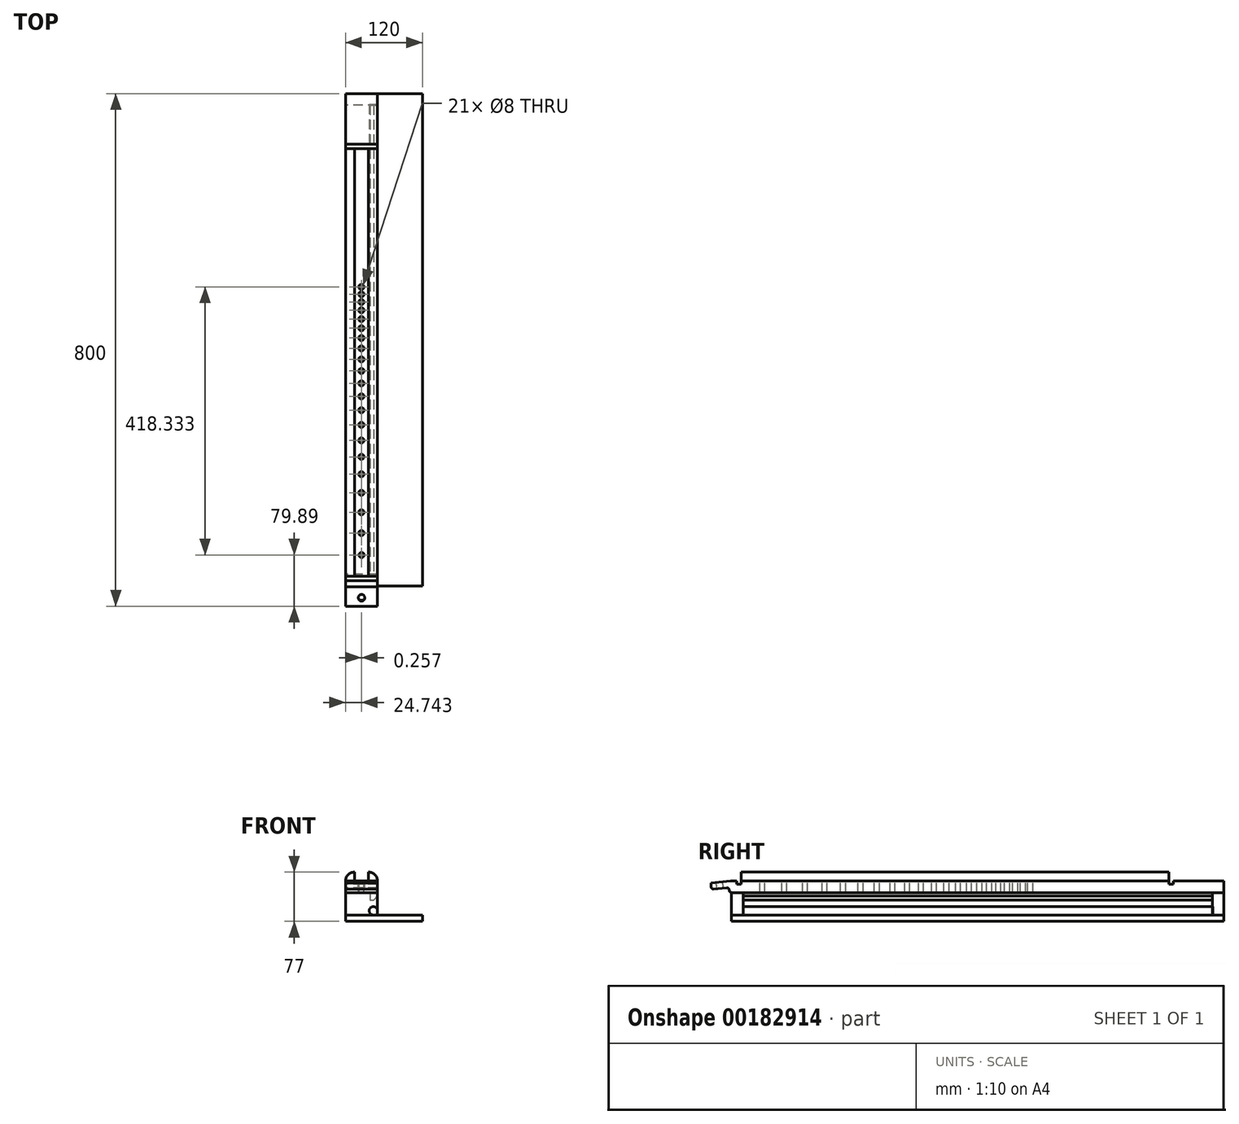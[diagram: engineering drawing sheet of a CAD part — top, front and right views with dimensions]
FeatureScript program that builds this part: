
annotation { "Feature Type Name" : "Feature", "Feature Type Description" : "" }
export const myFeature = defineFeature(function(context is Context, id is Id, definition is map)
    precondition{}
    {
        {
            var Q0;
            Q0=qCreatedBy(makeId("Front.planeOp"),FACE);
            var sketch = newSketch(context, id + "F0", { "sketchPlane" : qUnion([Q0])});
            skLineSegment(sketch, "E0.bottom", {"start": v(25, -9) * mm, "end": v(-25, -9) * mm});
            skLineSegment(sketch, "E0.top", {"start": v(25, 9) * mm, "end": v(-25, 9) * mm});
            skLineSegment(sketch, "E0.left", {"start": v(25, -9) * mm, "end": v(25, 9) * mm});
            skLineSegment(sketch, "E0.right", {"start": v(-25, -9) * mm, "end": v(-25, 9) * mm});
            skPoint(sketch, "E0.middle", {"position": v(0, 0) * mm});
            skSolve(sketch);
        }
        {
            var Q0;
            Q0=makeQuery(id+"F0.imprint","IMPRINT",FACE,{"disambiguationData":[TD([[makeQuery(id+"F0.imprint","IMPRINT",EDGE,{"derivedFrom":sQuery(id+"F0.wireOp",EDGE,"E0.bottom")}),-1.0]])]});
            extrude(context, id + "F1", {"entities" : qUnion([Q0]), "depth" : 800 * mm});
        }
        {
            var Q0;
            Q0=makeQuery(id+"F1.opExtrude","SWEPT_FACE",FACE,{"disambiguationData":[OSD([sQuery(id+"F0.wireOp",EDGE,"E0.top")])]});
            var sketch = newSketch(context, id + "F2", { "sketchPlane" : qUnion([Q0])});
            skLineSegment(sketch, "E1.bottom", {"start": v(25, -760) * mm, "end": v(-25, -760) * mm});
            skLineSegment(sketch, "E1.top", {"start": v(25, -753) * mm, "end": v(-25, -753) * mm});
            skLineSegment(sketch, "E1.left", {"start": v(25, -760) * mm, "end": v(25, -753) * mm});
            skLineSegment(sketch, "E1.right", {"start": v(-25, -760) * mm, "end": v(-25, -753) * mm});
            skPoint(sketch, "E1.middle", {"position": v(0, -756.5) * mm});
            skLineSegment(sketch, "E2", {"start": v(0, -800) * mm, "end": v(0, -797.81) * mm, "construction": true});
            skLineSegment(sketch, "E3.bottom", {"start": v(-25, -79) * mm, "end": v(25, -79) * mm});
            skLineSegment(sketch, "E3.top", {"start": v(-25, -86) * mm, "end": v(25, -86) * mm});
            skLineSegment(sketch, "E3.left", {"start": v(-25, -79) * mm, "end": v(-25, -86) * mm});
            skLineSegment(sketch, "E3.right", {"start": v(25, -79) * mm, "end": v(25, -86) * mm});
            skPoint(sketch, "E3.middle", {"position": v(0, -82.5) * mm});
            skLineSegment(sketch, "E4", {"start": v(0, -17.02) * mm, "end": v(0, -142.95) * mm, "construction": true});
            skSolve(sketch);
        }
        {
            var Q0;
            Q0=makeQuery(id+"F2.imprint","IMPRINT",FACE,{"disambiguationData":[TD([[makeQuery(id+"F2.imprint","IMPRINT",EDGE,{"derivedFrom":sQuery(id+"F2.wireOp",EDGE,"E3.bottom")}),-1.0]])]});
            var Q1;
            Q1=makeQuery(id+"F2.imprint","IMPRINT",FACE,{"disambiguationData":[TD([[makeQuery(id+"F2.imprint","IMPRINT",EDGE,{"derivedFrom":sQuery(id+"F2.wireOp",EDGE,"E1.bottom")}),-1.0]])]});
            extrude(context, id + "F3", {"entities" : qUnion([Q0, Q1]), "operationType" : NewBodyOperationType.REMOVE, "oppositeDirection" : true, "depth" : 5 * mm});
        }
        {
            var Q0;
            Q0=makeQuery(id+"F1.opExtrude","SWEPT_FACE",FACE,{"disambiguationData":[OSD([sQuery(id+"F0.wireOp",EDGE,"E0.left")])]});
            var sketch = newSketch(context, id + "F4", { "sketchPlane" : qUnion([Q0])});
            skLineSegment(sketch, "E5.bottom", {"start": v(-848.78, 6.5) * mm, "end": v(-818.88, 8.9) * mm, "construction": true});
            skLineSegment(sketch, "E5.right", {"start": v(-818.58, -0.8) * mm, "end": v(-816.95, -21.06) * mm, "construction": true});
            skSolve(sketch);
        }
        {
            var Q0;
            {var subQ0=sQuery(id+"F0.wireOp",EDGE,"E0.left");Q0=makeQuery(id+"F4.imprint","IMPRINT",FACE,{"disambiguationData":[TD([[makeQuery(id+"F4.imprint","IMPRINT",EDGE,{"derivedFrom":makeQuery(id+"F1.opExtrude","CAP_EDGE",EDGE,{"disambiguationData":[OSD([subQ0])],"isStart":true})}),1.0]])]});}
            var sketch = newSketch(context, id + "F5", { "sketchPlane" : qUnion([Q0])});
            skLineSegment(sketch, "E6", {"start": v(-772.1, -1.08) * mm, "end": v(-809.12, -4.9) * mm});
            skLineSegment(sketch, "E7", {"start": v(-809.12, -4.9) * mm, "end": v(-809.12, -19.23) * mm});
            skLineSegment(sketch, "E8", {"start": v(-809.12, -19.23) * mm, "end": v(-771.09, -19.23) * mm});
            skLineSegment(sketch, "E9", {"start": v(-771.09, -19.23) * mm, "end": v(-772.1, -1.08) * mm});
            skLineSegment(sketch, "E10", {"start": v(-804.66, 5.4) * mm, "end": v(-715.45, 14.6) * mm});
            skLineSegment(sketch, "E11", {"start": v(-715.45, 14.6) * mm, "end": v(-805.06, 14.6) * mm});
            skLineSegment(sketch, "E12", {"start": v(-804.66, 5.4) * mm, "end": v(-805.06, 14.6) * mm});
            skSolve(sketch);
        }
        {
            var Q0;
            Q0 = qSketchRegion(id + "F5", true);
            extrude(context, id + "F6", {"entities" : qUnion([Q0]), "operationType" : NewBodyOperationType.REMOVE, "endBound" : BoundingType.THROUGH_ALL, "oppositeDirection" : true, "depth" : 25 * mm});
        }
        {
            var Q0;
            Q0=makeQuery(id+"F6.boolean.opBoolean","COPY",FACE,{"derivedFrom":makeQuery(id+"F6.opExtrude","SWEPT_FACE",FACE,{"disambiguationData":[OSD([sQuery(id+"F5.wireOp",EDGE,"E10")])]})});
            var sketch = newSketch(context, id + "F7", { "sketchPlane" : qUnion([Q0])});
            skCircle(sketch, "E13", {"center": v(0, -1003.47) * mm, "radius": 4 * mm});
            skCircle(sketch, "E14", {"center": v(0, -782.06) * mm, "radius": 5.1 * mm});
            skPoint(sketch, "E15", {"position": v(0, -795.17) * mm});
            skSolve(sketch);
        }
        {
            var Q0;
            Q0 = qSketchRegion(id + "F7", true);
            extrude(context, id + "F8", {"entities" : qUnion([Q0]), "operationType" : NewBodyOperationType.REMOVE, "endBound" : BoundingType.THROUGH_ALL, "oppositeDirection" : true, "depth" : 25 * mm});
        }
        {
            var Q0;
            Q0=makeQuery(id+"F1.opExtrude","SWEPT_FACE",FACE,{"disambiguationData":[OSD([sQuery(id+"F0.wireOp",EDGE,"E0.top")])]});
            var sketch = newSketch(context, id + "F9", { "sketchPlane" : qUnion([Q0])});
            skSolve(sketch);
        }
        {
            var Q0;
            {var subQ0=sQuery(id+"F0.wireOp",EDGE,"E0.top");Q0=makeQuery(id+"F9.imprint","IMPRINT",FACE,{"disambiguationData":[TD([[makeQuery(id+"F9.imprint","IMPRINT",EDGE,{"derivedFrom":makeQuery(id+"F1.opExtrude","CAP_EDGE",EDGE,{"disambiguationData":[OSD([subQ0])],"isStart":true})}),1.0]])]});}
            var sketch = newSketch(context, id + "F10", { "sketchPlane" : qUnion([Q0])});
            skLineSegment(sketch, "E16", {"start": v(-24.54, -756.42) * mm, "end": v(24.02, -756.42) * mm, "construction": true});
            skLineSegment(sketch, "E17", {"start": v(-24.54, -366.18) * mm, "end": v(24.02, -366.18) * mm, "construction": true});
            skLineSegment(sketch, "E18", {"start": v(-24.54, -301.78) * mm, "end": v(24.02, -301.78) * mm, "construction": true});
            skLineSegment(sketch, "E19", {"start": v(-24.54, -313.22) * mm, "end": v(24.02, -313.22) * mm, "construction": true});
            skLineSegment(sketch, "E20", {"start": v(-24.54, -325.33) * mm, "end": v(24.02, -325.33) * mm, "construction": true});
            skLineSegment(sketch, "E21", {"start": v(-24.54, -338.17) * mm, "end": v(24.02, -338.17) * mm, "construction": true});
            skLineSegment(sketch, "E22", {"start": v(-24.54, -351.77) * mm, "end": v(24.02, -351.77) * mm, "construction": true});
            skLineSegment(sketch, "E23", {"start": v(-24.54, -381.45) * mm, "end": v(24.02, -381.45) * mm, "construction": true});
            skLineSegment(sketch, "E24", {"start": v(-24.54, -397.63) * mm, "end": v(24.02, -397.63) * mm, "construction": true});
            skLineSegment(sketch, "E25", {"start": v(-24.54, -414.77) * mm, "end": v(24.02, -414.77) * mm, "construction": true});
            skLineSegment(sketch, "E26", {"start": v(-24.54, -432.92) * mm, "end": v(24.02, -432.92) * mm, "construction": true});
            skLineSegment(sketch, "E27", {"start": v(-24.54, -452.16) * mm, "end": v(24.02, -452.16) * mm, "construction": true});
            skLineSegment(sketch, "E28", {"start": v(-24.54, -472.54) * mm, "end": v(24.02, -472.54) * mm, "construction": true});
            skLineSegment(sketch, "E29", {"start": v(-24.54, -494.13) * mm, "end": v(24.02, -494.13) * mm, "construction": true});
            skLineSegment(sketch, "E30", {"start": v(-24.54, -517) * mm, "end": v(24.02, -517) * mm, "construction": true});
            skLineSegment(sketch, "E31", {"start": v(-24.54, -541.24) * mm, "end": v(24.02, -541.24) * mm, "construction": true});
            skLineSegment(sketch, "E32", {"start": v(-24.54, -566.92) * mm, "end": v(24.02, -566.92) * mm, "construction": true});
            skLineSegment(sketch, "E33", {"start": v(-24.54, -594.13) * mm, "end": v(24.02, -594.13) * mm, "construction": true});
            skLineSegment(sketch, "E34", {"start": v(-24.54, -622.95) * mm, "end": v(24.02, -622.95) * mm, "construction": true});
            skLineSegment(sketch, "E35", {"start": v(-24.54, -653.48) * mm, "end": v(24.02, -653.48) * mm, "construction": true});
            skLineSegment(sketch, "E36", {"start": v(-24.54, -685.83) * mm, "end": v(24.02, -685.83) * mm, "construction": true});
            skLineSegment(sketch, "E37", {"start": v(-24.54, -720.11) * mm, "end": v(24.02, -720.11) * mm, "construction": true});
            skSolve(sketch);
        }
        {
            var Q0;
            {var subQ0=sQuery(id+"F0.wireOp",EDGE,"E0.top");Q0=makeQuery(id+"F9.imprint","IMPRINT",FACE,{"disambiguationData":[TD([[makeQuery(id+"F9.imprint","IMPRINT",EDGE,{"derivedFrom":makeQuery(id+"F1.opExtrude","CAP_EDGE",EDGE,{"disambiguationData":[OSD([subQ0])],"isStart":true})}),1.0]])]});}
            var sketch = newSketch(context, id + "F11", { "sketchPlane" : qUnion([Q0])});
            skCircle(sketch, "E38", {"center": v(0, 548.49) * mm, "radius": 5 * mm});
            skCircle(sketch, "E39", {"center": v(0, 720.4) * mm, "radius": 5 * mm});
            skCircle(sketch, "E40", {"center": v(0, -720.11) * mm, "radius": 4 * mm});
            skCircle(sketch, "E41", {"center": v(-0.26, -685.83) * mm, "radius": 4 * mm});
            skCircle(sketch, "E42", {"center": v(-0.26, -653.48) * mm, "radius": 4 * mm});
            skCircle(sketch, "E43", {"center": v(-0.26, -622.95) * mm, "radius": 4 * mm});
            skCircle(sketch, "E44", {"center": v(-0.26, -594.13) * mm, "radius": 4 * mm});
            skCircle(sketch, "E45", {"center": v(-0.26, -566.92) * mm, "radius": 4 * mm});
            skCircle(sketch, "E46", {"center": v(-0.26, -541.24) * mm, "radius": 4 * mm});
            skCircle(sketch, "E47", {"center": v(-0.26, -517) * mm, "radius": 4 * mm});
            skCircle(sketch, "E48", {"center": v(-0.26, -494.13) * mm, "radius": 4 * mm});
            skCircle(sketch, "E49", {"center": v(-0.26, -472.54) * mm, "radius": 4 * mm});
            skCircle(sketch, "E50", {"center": v(-0.26, -452.16) * mm, "radius": 4 * mm});
            skCircle(sketch, "E51", {"center": v(-0.26, -432.92) * mm, "radius": 4 * mm});
            skCircle(sketch, "E52", {"center": v(-0.26, -414.77) * mm, "radius": 4 * mm});
            skCircle(sketch, "E53", {"center": v(-0.26, -397.63) * mm, "radius": 4 * mm});
            skCircle(sketch, "E54", {"center": v(-0.26, -381.45) * mm, "radius": 4 * mm});
            skCircle(sketch, "E55", {"center": v(-0.26, -366.18) * mm, "radius": 4 * mm});
            skCircle(sketch, "E56", {"center": v(-0.26, -351.77) * mm, "radius": 4 * mm});
            skCircle(sketch, "E57", {"center": v(-0.26, -338.17) * mm, "radius": 4 * mm});
            skCircle(sketch, "E58", {"center": v(-0.26, -325.33) * mm, "radius": 4 * mm});
            skCircle(sketch, "E59", {"center": v(-0.26, -313.22) * mm, "radius": 4 * mm});
            skCircle(sketch, "E60", {"center": v(-0.26, -301.78) * mm, "radius": 4 * mm});
            skSolve(sketch);
        }
        {
            var Q0;
            Q0 = qSketchRegion(id + "F11", true);
            extrude(context, id + "F12", {"entities" : qUnion([Q0]), "operationType" : NewBodyOperationType.REMOVE, "oppositeDirection" : true, "depth" : 25 * mm});
        }
        {
            var Q0;
            Q0=qCreatedBy(makeId("Front.planeOp"),FACE);
            var sketch = newSketch(context, id + "F13", { "sketchPlane" : qUnion([Q0])});
            skLineSegment(sketch, "E61.top", {"start": v(-25, 9) * mm, "end": v(-11, 9) * mm});
            skLineSegment(sketch, "E61.right", {"start": v(-11, 23) * mm, "end": v(-11, 9) * mm});
            skArc(sketch, "E62", {"start": v(-11, 23) * mm, "mid": v(-20.9, 18.9) * mm, "end": v(-25, 9) * mm});
            skLineSegment(sketch, "E63.MirrorCS", {"start": v(11, 23) * mm, "end": v(11, 9) * mm});
            skLineSegment(sketch, "E64.MirrorCS", {"start": v(25, 9) * mm, "end": v(11, 9) * mm});
            skArc(sketch, "E65.MirrorCS", {"start": v(11, 23) * mm, "mid": v(20.9, 18.9) * mm, "end": v(25, 9) * mm});
            skSolve(sketch);
        }
        {
            var Q0;
            Q0 = qSketchRegion(id + "F13", true);
            extrude(context, id + "F14", {"entities" : qUnion([Q0]), "depth" : 753 * mm});
        }
        {
            var Q0;
            Q0 = qSketchRegion(id + "F13", true);
            extrude(context, id + "F15", {"entities" : qUnion([Q0]), "operationType" : NewBodyOperationType.REMOVE, "depth" : 86 * mm});
        }
        {
            var Q0;
            Q0=makeQuery(id+"F6.boolean.opBoolean","COPY",EDGE,{"derivedFrom":makeQuery(id+"F6.opExtrude","SWEPT_EDGE",EDGE,{"disambiguationData":[OSD([sQuery(id+"F5.wireOp",EDGE,"E6"),sQuery(id+"F5.wireOp",EDGE,"E9")])]})});
            var Q1;
            Q1=makeQuery(id+"F6.boolean.opBoolean","INTERSECT",EDGE,{"derivedFrom":[makeQuery(id+"F1.opExtrude","SWEPT_FACE",FACE,{"disambiguationData":[OSD([sQuery(id+"F0.wireOp",EDGE,"E0.bottom")])]}),makeQuery(id+"F6.opExtrude","SWEPT_FACE",FACE,{"disambiguationData":[OSD([sQuery(id+"F5.wireOp",EDGE,"E9")])]})]});
            var Q2;
            Q2=makeQuery(id+"F6.boolean.opBoolean","INTERSECT",EDGE,{"derivedFrom":[makeQuery(id+"F1.opExtrude","CAP_FACE",FACE,{"disambiguationData":[OSD([sQuery(id+"F0.wireOp",EDGE,"E0.bottom"),sQuery(id+"F0.wireOp",EDGE,"E0.top"),sQuery(id+"F0.wireOp",EDGE,"E0.left"),sQuery(id+"F0.wireOp",EDGE,"E0.right")])],"isStart":false}),makeQuery(id+"F6.opExtrude","SWEPT_FACE",FACE,{"disambiguationData":[OSD([sQuery(id+"F5.wireOp",EDGE,"E6")])]})]});
            fillet(context, id + "F16", {"entities" : qUnion([Q0, Q1, Q2]), "radius" : 3.6 * mm, "tangentPropagation" : true, "allowEdgeOverflow" : false});
        }
        {
            var Q0;
            Q0=qCreatedBy(makeId("Front.planeOp"),FACE);
            var sketch = newSketch(context, id + "F17", { "sketchPlane" : qUnion([Q0])});
            skLineSegment(sketch, "E66.bottom", {"start": v(25, -9) * mm, "end": v(-25, -9) * mm});
            skLineSegment(sketch, "E66.top", {"start": v(25, -44) * mm, "end": v(-25, -44) * mm});
            skLineSegment(sketch, "E66.right", {"start": v(-25, -9) * mm, "end": v(-25, -44) * mm});
            skLineSegment(sketch, "E67.MirrorCS", {"start": v(25, -9) * mm, "end": v(25, -44) * mm});
            skSolve(sketch);
        }
        {
            var Q0;
            Q0 = qSketchRegion(id + "F17", true);
            extrude(context, id + "F18", {"entities" : qUnion([Q0]), "depth" : 18 * mm});
        }
        {
            var Q0;
            Q0=makeQuery(id+"F1.opExtrude","SWEPT_FACE",FACE,{"disambiguationData":[OSD([sQuery(id+"F0.wireOp",EDGE,"E0.bottom")])]});
            var sketch = newSketch(context, id + "F19", { "sketchPlane" : qUnion([Q0])});
            skLineSegment(sketch, "E68.bottom", {"start": v(25, 768.25) * mm, "end": v(-25, 768.25) * mm});
            skLineSegment(sketch, "E68.top", {"start": v(25, 750.25) * mm, "end": v(-25, 750.25) * mm});
            skLineSegment(sketch, "E68.left", {"start": v(25, 768.25) * mm, "end": v(25, 750.25) * mm});
            skLineSegment(sketch, "E68.right", {"start": v(-25, 768.25) * mm, "end": v(-25, 750.25) * mm});
            skSolve(sketch);
        }
        {
            var Q0;
            Q0 = qSketchRegion(id + "F19", true);
            extrude(context, id + "F20", {"entities" : qUnion([Q0]), "depth" : 35 * mm});
        }
        {
            var Q0;
            Q0=makeQuery(id+"F20.opExtrude","SWEPT_FACE",FACE,{"disambiguationData":[OSD([sQuery(id+"F19.wireOp",EDGE,"E68.top")])]});
            var sketch = newSketch(context, id + "F21", { "sketchPlane" : qUnion([Q0])});
            skCircle(sketch, "E69", {"center": v(-18.5, -37.5) * mm, "radius": 6.5 * mm});
            skSolve(sketch);
        }
        {
            var Q0;
            Q0 = qSketchRegion(id + "F21", true);
            var Q1;
            Q1 = qConstructionFilter(qBodyType(qCreatedBy(id + "F21" ,EDGE), BodyType.WIRE), ConstructionObject.NO);
            extrude(context, id + "F22", {"entities" : qUnion([Q0]), "surfaceEntities" : qUnion([Q1]), "depth" : 733 * mm});
        }
        {
            var Q0;
            Q0=makeQuery(id+"F20.opExtrude","SWEPT_FACE",FACE,{"disambiguationData":[OSD([sQuery(id+"F19.wireOp",EDGE,"E68.bottom")])]});
            var sketch = newSketch(context, id + "F23", { "sketchPlane" : qUnion([Q0])});
            skLineSegment(sketch, "E70.bottom", {"start": v(-25, -44) * mm, "end": v(95, -44) * mm});
            skLineSegment(sketch, "E70.top", {"start": v(-25, -54) * mm, "end": v(95, -54) * mm});
            skLineSegment(sketch, "E70.left", {"start": v(-25, -44) * mm, "end": v(-25, -54) * mm});
            skLineSegment(sketch, "E70.right", {"start": v(95, -44) * mm, "end": v(95, -54) * mm});
            skSolve(sketch);
        }
        {
            var Q0;
            Q0=makeQuery(id+"F23.imprint","IMPRINT",FACE,{"disambiguationData":[TD([[makeQuery(id+"F23.imprint","IMPRINT",EDGE,{"derivedFrom":sQuery(id+"F23.wireOp",EDGE,"E70.bottom")}),1.0]])]});
            extrude(context, id + "F24", {"entities" : qUnion([Q0]), "oppositeDirection" : true, "depth" : 768 * mm});
        }
        {
            var Q0;
            Q0=makeQuery(id+"F20.opExtrude","SWEPT_FACE",FACE,{"disambiguationData":[OSD([sQuery(id+"F19.wireOp",EDGE,"E68.top")])]});
            var sketch = newSketch(context, id + "F25", { "sketchPlane" : qUnion([Q0])});
            skLineSegment(sketch, "E71.bottom", {"start": v(-13.5, -9) * mm, "end": v(-25, -9) * mm});
            skLineSegment(sketch, "E71.top", {"start": v(-13.5, -20.5) * mm, "end": v(-25, -20.5) * mm});
            skLineSegment(sketch, "E71.left", {"start": v(-13.5, -9) * mm, "end": v(-13.5, -20.5) * mm});
            skLineSegment(sketch, "E71.right", {"start": v(-25, -9) * mm, "end": v(-25, -20.5) * mm});
            skSolve(sketch);
        }
        {
            var Q0;
            Q0 = qSketchRegion(id + "F25", true);
            extrude(context, id + "F26", {"entities" : qUnion([Q0]), "depth" : 732.3 * mm});
        }
        {
            var Q0;
            Q0=makeQuery(id+"F26.opExtrude","SWEPT_EDGE",EDGE,{"disambiguationData":[OSD([sQuery(id+"F0.wireOp",EDGE,"E0.bottom"),sQuery(id+"F0.wireOp",EDGE,"E0.left"),sQuery(id+"F19.wireOp",EDGE,"E68.top"),sQuery(id+"F19.wireOp",EDGE,"E68.left"),sQuery(id+"F25.wireOp",EDGE,"E71.top"),sQuery(id+"F25.wireOp",EDGE,"E71.right")])]});
            chamfer(context, id + "F27", {"entities" : qUnion([Q0]), "width" : 6 * mm, "tangentPropagation" : true});
        }
    });
